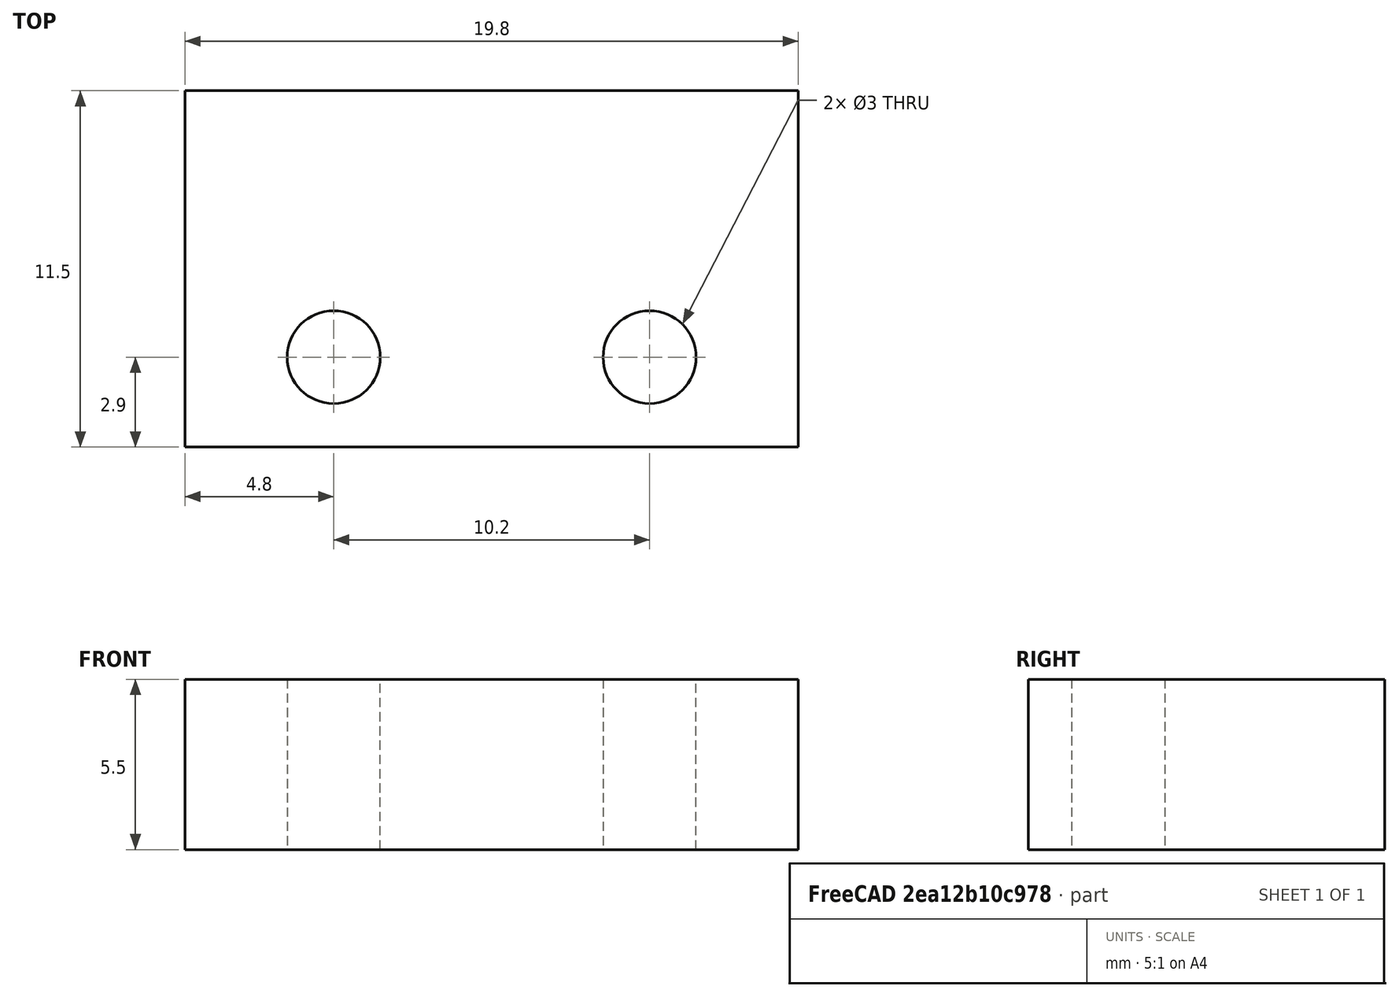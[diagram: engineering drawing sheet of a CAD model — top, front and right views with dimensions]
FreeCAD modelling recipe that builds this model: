
FCSTD DOCUMENT  (FreeCAD 0.16R6707 (Git))
Label: support_fc_pince_secondaire
License: All rights reserved
LicenseURL: http://en.wikipedia.org/wiki/All_rights_reserved
objects: Sketcher::SketchObject×1, PartDesign::Pad×1
note: 3 computed .brp shape members not serialized (recipe doc carries the construction recipe); baked Part::Feature solids carry a one-line shape summary decoded from their .brp

FEATURE [Sketcher::SketchObject] Sketch
  sketch-geometry (6):
    g0: LineSegment StartX=0 StartY=0 StartZ=0 EndX=19.8 EndY=0 EndZ=0
    g1: LineSegment StartX=19.8 StartY=0 StartZ=0 EndX=19.8 EndY=11.5 EndZ=0
    g2: LineSegment StartX=19.8 StartY=11.5 StartZ=0 EndX=0 EndY=11.5 EndZ=0
    g3: LineSegment StartX=0 StartY=11.5 StartZ=0 EndX=0 EndY=0 EndZ=0
    g4: Circle CenterX=4.8 CenterY=2.9 CenterZ=0 NormalX=0 NormalY=0 NormalZ=1 Radius=1.5
    g5: Circle CenterX=15 CenterY=2.9 CenterZ=0 NormalX=0 NormalY=0 NormalZ=1 Radius=1.5
  constraints (17):
    c: Coincident(g0,g1)
    c: Coincident(g1,g2)
    c: Coincident(g2,g3)
    c: Coincident(g3,g0)
    c: Horizontal(g0)
    c: Horizontal(g2)
    c: Vertical(g1)
    c: Vertical(g3)
    c: Coincident(g0,g-1)
    c: Distance(g3) = 11.5
    c: Distance(g2) = 19.8
    c: DistanceY(g4,g5) = 0
    c: DistanceX(g4,g5) = 10.2
    c: DistanceX(g4) = 4.8
    c: Radius(g4) = 1.5
    c: Equal(g4,g5)
    c: DistanceY(g4) = 2.9
FEATURE [PartDesign::Pad] Pad
  Length = 5.5
  Length2 = 100
  Sketch = -> Sketch
  Type = 0
